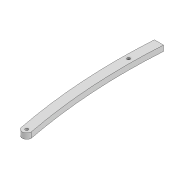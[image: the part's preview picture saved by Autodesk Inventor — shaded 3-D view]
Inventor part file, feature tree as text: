
AUTODESK INVENTOR PART (.ipt)
format: ipt  version: 2022 (Build 260153000, 153)  size: 110,592 bytes
history: native  units: mm
features: extrude x2, sketch x1
ambient origin geometry x8: Origin, YZ Plane, XZ Plane, XY Plane, X Axis, Y Axis, Z Axis, Center Point
bodies: Solid1 (feature_tree)
feature tree (3):
  extrude  "Extrusion1"  Depth=10.0mm
  extrude  "Extrusion2"  Depth=10.0mm
  sketch  "Sketch2"  dims[d0=3.3mm d1=3.3mm d2=10.0mm d3=288.984mm d6=6.0mm d7=0.0mm d14=3.3mm d15=231.585mm d18=600.0mm d19=600.0mm d20=3.3mm d21=122.909mm d22=10.0mm d23=0.0mm]
